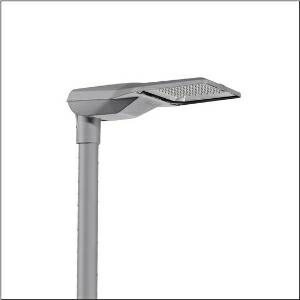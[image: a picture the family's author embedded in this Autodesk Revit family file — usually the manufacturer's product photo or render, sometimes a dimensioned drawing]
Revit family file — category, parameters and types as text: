
# Revit family: streetlight_sl_21_iq_midi___st1_0a_5xe3d61g08nb_ea68
name_source: partatom
category: Lighting Fixtures
units: mm (PartAtom-declared; Revit-internal decimal feet)

## family parameters
Cut with Voids When Loaded = No
Host = Face
Light Source = No
Part Type = Normal
Room Calculation Point = No
Round Connector Dimension = Use Diameter
Shared = No

## types (1)
- --- (1 x LED, 20820 lm, 155.5 W, 2700K)
    Apparent Load = 155 VA
    CIE Flux Codes = 40 73 97 100 100
    Color Rendering = 70
    Color Temperature = 2700K
    Default Elevation = 1800 mm
    Description = Streetlight SL 21 iQ midi, mast luminaire, primary light control with lens, of PMMA, primary optical cover: cover, of toughened safety glass, transparent, light distribution: ST1.0a, light emission: direct distribution, primary light characteristic: asymmetric, installation type: post-top, side-entry, LED, High Power LED, rated luminous flux: 20.820lm, luminous efficacy: 134lm/W, light colour: 727, colour temperature: 2700K, control gear: iQ Street-Remote, control: Street-Remote, Auto-Match, Temp-Guard, Lumen-Switch, Night-Set, Smart-Wire, Light-Fading, Desk-Remote (wireless, voltage-free reading and setting of iQ features in the workshop via application-optimized NFC function/RFID function), optimised constant luminous flux control (CLO 2.0), pre-setting: linear dimming characteristic, mains connection: 230..240V, AC, 50/60Hz, start of lifetime: 156W, end of service life: 162W, reduction: 69W, luminaire housing, of diecast aluminium, powder-coated, Siteco® metallic grey (DB 702S), corrosivity category C5 mid according to DIN EN ISO 12944, please order mast flange separately, inclination adjustable: 0°, 5°, 10°, 15°, sealing non-destructively replaceable, multi-level sealing system, length: 644mm, width: 335mm, height: 110mm, mast flange for spigot size: 42mm (side-entry): 5XC10008XM4, 60/48mm (side-entry/post-top): 5XC10108XM2, 76/60mm (side-entry/post-top): 5XC10108XM1, mounting height: 4..8m, protection rating (complete): IP66, insulation class (complete): insulation class II (safety insulation), certification: CE, ENEC, ENEC+, VDE, impact resistance: IK10, permissible operating ambient temperature for outdoor applications: -40..+50°C, standard-compliant lighting for roads and squares, packaging unit: 1 piece

Light Distribution: ST1.0a
    Height = 111 mm
    Lamp = 1 x LED
    Lamp Light Flux = 20820 lm
    Lamp Power = 155.5 W
    Lamp count = 1
    Length = 644 mm
    Luminous efficacy = 134 lm/W
    Manufacturer = Siteco
    ModVariant = No
    Model = 5XE3D61G08NB
    Number of Poles = 1
    OnlyDefault = Yes
    Power Factor = 1
    Product Name = Streetlight SL 21 iQ midi | ST1.0a
    Product group = mast luminaire | pylon top
    ProductGroupID = 6100
    Protection Class = Protection class II
    Protection Degree = IP 66
    RLX_Detail_Level = 1
    RLX_Emergency_Light_Flux = 0 lm
    RLX_Emergency_Type = 0
    RLX_Emergency_Type_DB = No
    RlxData = <blob elided: 27193 chars, md5=c1833685>
    Socket = socket
    Standby Power = 0 W
    System Light Flux = 20820 lm
    System Power = 155 W
    Type Comments = factory setting: luminous flux: 100 % | dim-lin: 254 | 823 mA
    Type Image = l_1004298.jpg
    URL = http://relux.com
    VarID = @adj_192155
    Voltage = 0 V
    Weight = 0.00 kg
    Width = 336 mm

## geometry (parser evidence)
native form markers: Blend x4, Sweep x12
no freeform markers — native parametric forms only
